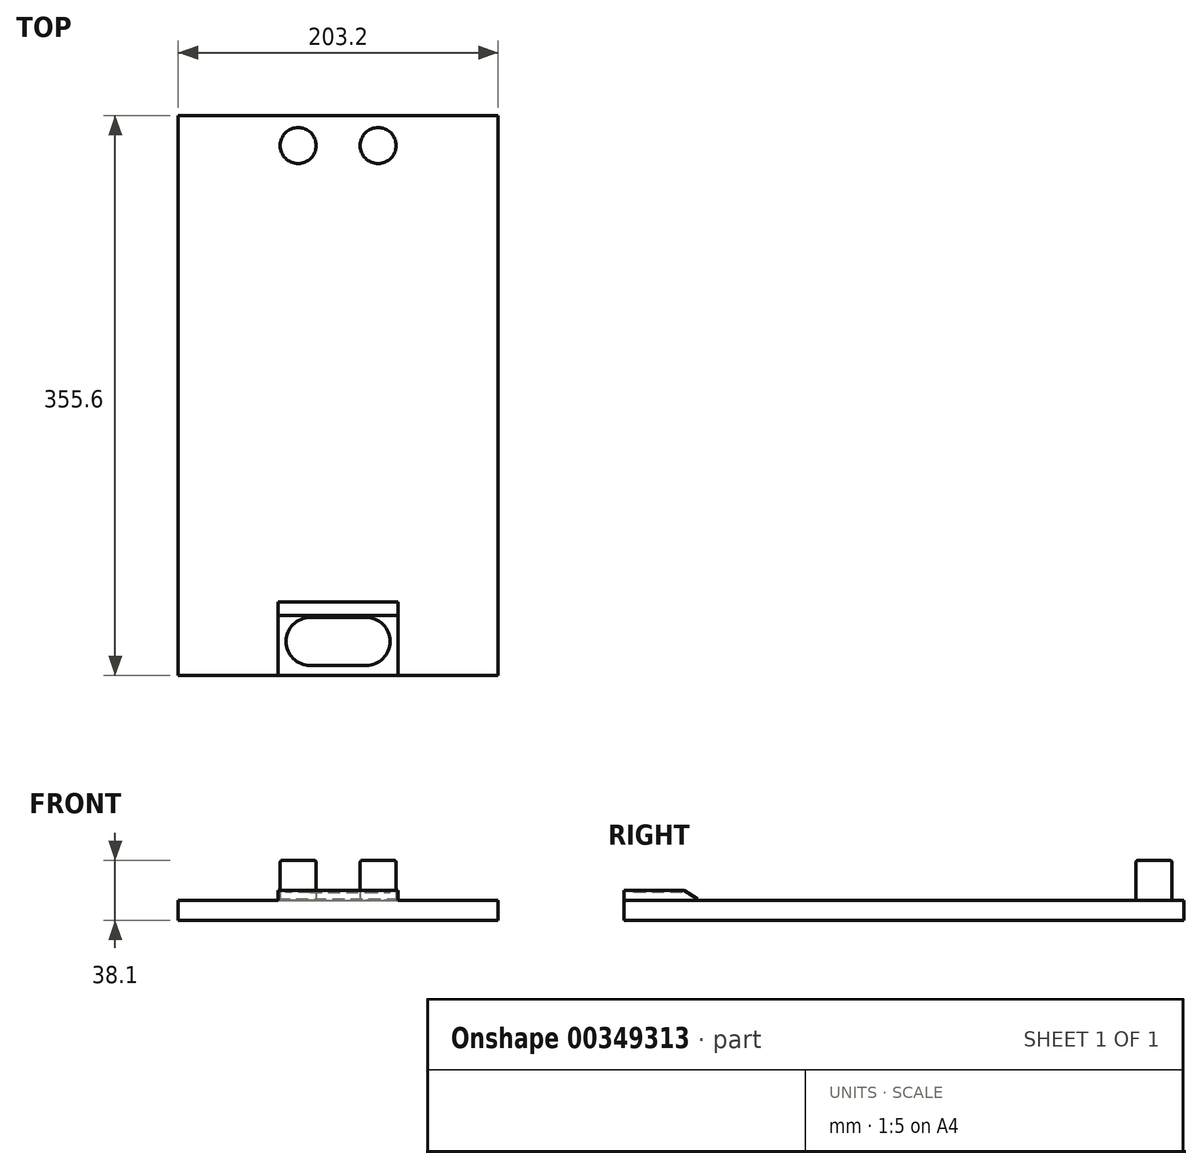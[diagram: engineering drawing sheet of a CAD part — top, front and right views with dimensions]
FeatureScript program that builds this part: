
annotation { "Feature Type Name" : "Feature", "Feature Type Description" : "" }
export const myFeature = defineFeature(function(context is Context, id is Id, definition is map)
    precondition{}
    {
        {
            var Q0;
            Q0=qCreatedBy(makeId("Top.planeOp"),FACE);
            var sketch = newSketch(context, id + "F0", { "sketchPlane" : qUnion([Q0])});
            skLineSegment(sketch, "E0.bottom", {"start": v(0, 0) * mm, "end": v(203.2, 0) * mm});
            skLineSegment(sketch, "E0.top", {"start": v(0, 355.6) * mm, "end": v(203.2, 355.6) * mm});
            skLineSegment(sketch, "E0.left", {"start": v(0, 0) * mm, "end": v(0, 355.6) * mm});
            skLineSegment(sketch, "E0.right", {"start": v(203.2, 0) * mm, "end": v(203.2, 355.6) * mm});
            skSolve(sketch);
        }
        {
            var Q0;
            Q0 = qSketchRegion(id + "F0", true);
            extrude(context, id + "F1", {"entities" : qUnion([Q0]), "depth" : 12.7 * mm});
        }
        {
            var Q0;
            Q0=makeQuery(id+"F0.imprint","IMPRINT",FACE,{"disambiguationData":[TD([[makeQuery(id+"F0.imprint","IMPRINT",EDGE,{"derivedFrom":sQuery(id+"F0.wireOp",EDGE,"E0.top")}),-1.0]])]});
            var sketch = newSketch(context, id + "F2", { "sketchPlane" : qUnion([Q0])});
            skCircle(sketch, "E1", {"center": v(76.2, 336.55) * mm, "radius": 11.43 * mm});
            skCircle(sketch, "E2", {"center": v(127, 336.55) * mm, "radius": 11.43 * mm});
            skSolve(sketch);
        }
        {
            var Q0;
            Q0 = qSketchRegion(id + "F2", true);
            extrude(context, id + "F3", {"entities" : qUnion([Q0]), "operationType" : NewBodyOperationType.ADD, "depth" : 38.1 * mm});
        }
        {
            var Q0;
            Q0=makeQuery(id+"F1.opExtrude","CAP_FACE",FACE,{"disambiguationData":[OSD([sQuery(id+"F0.wireOp",EDGE,"E0.bottom"),sQuery(id+"F0.wireOp",EDGE,"E0.top"),sQuery(id+"F0.wireOp",EDGE,"E0.left"),sQuery(id+"F0.wireOp",EDGE,"E0.right")])],"isStart":false});
            var sketch = newSketch(context, id + "F4", { "sketchPlane" : qUnion([Q0])});
            skLineSegment(sketch, "E3", {"start": v(63.5, 0) * mm, "end": v(63.5, 38.1) * mm});
            skLineSegment(sketch, "E4", {"start": v(63.5, 38.1) * mm, "end": v(139.7, 38.1) * mm});
            skLineSegment(sketch, "E5", {"start": v(139.7, 38.1) * mm, "end": v(139.7, 0) * mm});
            skLineSegment(sketch, "E6", {"start": v(139.7, 0) * mm, "end": v(63.5, 0) * mm});
            skSolve(sketch);
        }
        {
            var Q0;
            Q0 = qSketchRegion(id + "F4", true);
            extrude(context, id + "F5", {"entities" : qUnion([Q0]), "operationType" : NewBodyOperationType.ADD, "depth" : 6.35 * mm});
        }
        {
            var Q0;
            Q0=makeQuery(id+"F5.opExtrude","CAP_FACE",FACE,{"disambiguationData":[OSD([sQuery(id+"F4.wireOp",EDGE,"E3"),sQuery(id+"F4.wireOp",EDGE,"E4"),sQuery(id+"F4.wireOp",EDGE,"E5"),sQuery(id+"F4.wireOp",EDGE,"E6")])],"isStart":false});
            var sketch = newSketch(context, id + "F6", { "sketchPlane" : qUnion([Q0])});
            skLineSegment(sketch, "E7", {"start": v(83.82, 36.83) * mm, "end": v(119.38, 36.83) * mm});
            skLineSegment(sketch, "E8", {"start": v(83.82, 6.35) * mm, "end": v(119.38, 6.35) * mm});
            skArc(sketch, "E9", {"start": v(83.82, 36.83) * mm, "mid": v(68.58, 21.59) * mm, "end": v(83.82, 6.35) * mm});
            skArc(sketch, "E10", {"start": v(119.38, 36.83) * mm, "mid": v(134.62, 21.59) * mm, "end": v(119.38, 6.35) * mm});
            skSolve(sketch);
        }
        {
            var Q0;
            Q0 = qSketchRegion(id + "F6", true);
            extrude(context, id + "F7", {"entities" : qUnion([Q0]), "operationType" : NewBodyOperationType.REMOVE, "oppositeDirection" : true, "depth" : 1.27 * mm});
        }
        {
            var Q0;
            Q0=makeQuery(id+"F5.opExtrude","SWEPT_FACE",FACE,{"disambiguationData":[OSD([sQuery(id+"F4.wireOp",EDGE,"E5")])]});
            var sketch = newSketch(context, id + "F8", { "sketchPlane" : qUnion([Q0])});
            skLineSegment(sketch, "E11", {"start": v(38.1, 19.05) * mm, "end": v(38.1, 12.7) * mm});
            skLineSegment(sketch, "E12", {"start": v(38.1, 12.7) * mm, "end": v(46.69, 12.7) * mm});
            skLineSegment(sketch, "E13", {"start": v(46.69, 13.68) * mm, "end": v(38.1, 19.05) * mm});
            skLineSegment(sketch, "E14", {"start": v(46.69, 13.68) * mm, "end": v(46.69, 12.7) * mm});
            skSolve(sketch);
        }
        {
            var Q0;
            Q0 = qSketchRegion(id + "F8", true);
            extrude(context, id + "F9", {"entities" : qUnion([Q0]), "operationType" : NewBodyOperationType.ADD, "oppositeDirection" : true, "depth" : 76.2 * mm});
        }
        {
            var Q0;
            Q0=makeQuery(id+"F3.opExtrude","CAP_EDGE",EDGE,{"disambiguationData":[OSD([sQuery(id+"F2.wireOp",EDGE,"E1")])],"isStart":false});
            var Q1;
            Q1=makeQuery(id+"F3.opExtrude","CAP_EDGE",EDGE,{"disambiguationData":[OSD([sQuery(id+"F2.wireOp",EDGE,"E2")])],"isStart":false});
            fillet(context, id + "F10", {"entities" : qUnion([Q0, Q1]), "radius" : 1.27 * mm, "tangentPropagation" : true, "allowEdgeOverflow" : false});
        }
    });
